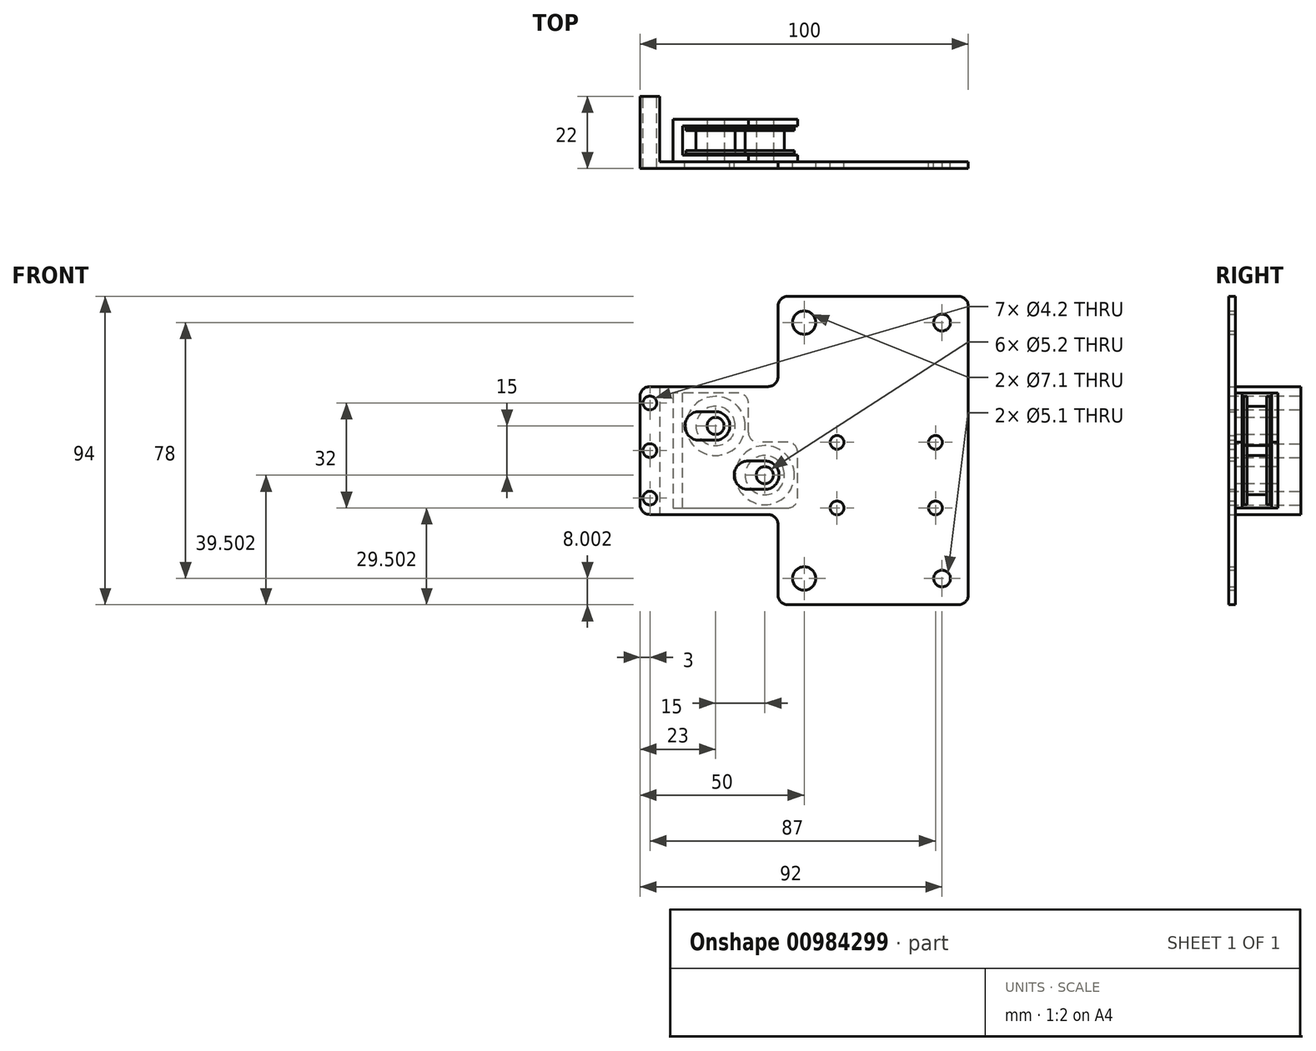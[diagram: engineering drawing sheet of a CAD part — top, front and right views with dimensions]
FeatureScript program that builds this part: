
annotation { "Feature Type Name" : "Feature", "Feature Type Description" : "" }
export const myFeature = defineFeature(function(context is Context, id is Id, definition is map)
    precondition{}
    {
        {
            var Q0;
            Q0=qCreatedBy(makeId("Front.planeOp"),FACE);
            var sketch = newSketch(context, id + "F0", { "sketchPlane" : qUnion([Q0])});
            skCircle(sketch, "E0", {"center": v(-21, 47.4) * mm, "radius": 3.55 * mm});
            skCircle(sketch, "E1", {"center": v(-21, -30.6) * mm, "radius": 3.55 * mm});
            skCircle(sketch, "E2", {"center": v(21, -30.6) * mm, "radius": 2.55 * mm});
            skCircle(sketch, "E3", {"center": v(21, 47.4) * mm, "radius": 2.55 * mm});
            skCircle(sketch, "E4", {"center": v(-11, 10.9) * mm, "radius": 2.1 * mm});
            skCircle(sketch, "E5", {"center": v(-11, -9.1) * mm, "radius": 2.1 * mm});
            skCircle(sketch, "E6", {"center": v(19, -9.1) * mm, "radius": 2.1 * mm});
            skCircle(sketch, "E7", {"center": v(19, 10.9) * mm, "radius": 2.1 * mm});
            skLineSegment(sketch, "E8", {"start": v(26, 55.4) * mm, "end": v(-26, 55.4) * mm});
            skLineSegment(sketch, "E9", {"start": v(-29, 52.4) * mm, "end": v(-29, 30.9) * mm});
            skLineSegment(sketch, "E10", {"start": v(-32, 27.9) * mm, "end": v(-68, 27.9) * mm});
            skLineSegment(sketch, "E11", {"start": v(-71, 24.9) * mm, "end": v(-71, -8.1) * mm});
            skLineSegment(sketch, "E12", {"start": v(-68, -11.1) * mm, "end": v(-32, -11.1) * mm});
            skLineSegment(sketch, "E13", {"start": v(-29, -14.1) * mm, "end": v(-29, -35.6) * mm});
            skLineSegment(sketch, "E14", {"start": v(-26, -38.6) * mm, "end": v(26, -38.6) * mm});
            skLineSegment(sketch, "E15", {"start": v(29, -35.6) * mm, "end": v(29, 52.4) * mm});
            skArc(sketch, "E16", {"start": v(-53, 20.24) * mm, "mid": v(-57.35, 15.9) * mm, "end": v(-53, 11.54) * mm});
            skArc(sketch, "E17", {"start": v(-48, 11.54) * mm, "mid": v(-43.65, 15.9) * mm, "end": v(-48, 20.24) * mm});
            skLineSegment(sketch, "E18", {"start": v(-53, 11.54) * mm, "end": v(-48, 11.54) * mm});
            skLineSegment(sketch, "E19", {"start": v(-53, 20.24) * mm, "end": v(-48, 20.24) * mm});
            skArc(sketch, "E20", {"start": v(-38, 5.24) * mm, "mid": v(-42.35, 0.9) * mm, "end": v(-38, -3.46) * mm});
            skArc(sketch, "E21", {"start": v(-33, -3.46) * mm, "mid": v(-28.65, 0.9) * mm, "end": v(-33, 5.24) * mm});
            skLineSegment(sketch, "E22", {"start": v(-38, 5.24) * mm, "end": v(-33, 5.24) * mm});
            skLineSegment(sketch, "E23", {"start": v(-33, -3.46) * mm, "end": v(-38, -3.46) * mm});
            skCircle(sketch, "E24", {"center": v(-68, 22.9) * mm, "radius": 2.1 * mm});
            skCircle(sketch, "E25", {"center": v(-68, 8.4) * mm, "radius": 2.1 * mm});
            skCircle(sketch, "E26", {"center": v(-68, -6.1) * mm, "radius": 2.1 * mm});
            skPoint(sketch, "E27.visualSharp", {"position": v(-71, 27.9) * mm});
            skArc(sketch, "E27.filletArc", {"start": v(-68, 27.9) * mm, "mid": v(-70.12, 27.01) * mm, "end": v(-71, 24.9) * mm});
            skPoint(sketch, "E28.visualSharp", {"position": v(-71, -11.1) * mm});
            skArc(sketch, "E28.filletArc", {"start": v(-71, -8.1) * mm, "mid": v(-70.12, -10.23) * mm, "end": v(-68, -11.1) * mm});
            skPoint(sketch, "E29.visualSharp", {"position": v(-29, -11.1) * mm});
            skArc(sketch, "E29.filletArc", {"start": v(-29, -14.1) * mm, "mid": v(-29.88, -11.99) * mm, "end": v(-32, -11.1) * mm});
            skPoint(sketch, "E30.visualSharp", {"position": v(-29, -38.6) * mm});
            skArc(sketch, "E30.filletArc", {"start": v(-29, -35.6) * mm, "mid": v(-28.12, -37.73) * mm, "end": v(-26, -38.6) * mm});
            skPoint(sketch, "E31.visualSharp", {"position": v(29, -38.6) * mm});
            skArc(sketch, "E31.filletArc", {"start": v(26, -38.6) * mm, "mid": v(28.12, -37.73) * mm, "end": v(29, -35.6) * mm});
            skPoint(sketch, "E32.visualSharp", {"position": v(29, 55.4) * mm});
            skArc(sketch, "E32.filletArc", {"start": v(29, 52.4) * mm, "mid": v(28.12, 54.51) * mm, "end": v(26, 55.4) * mm});
            skPoint(sketch, "E33.visualSharp", {"position": v(-29, 55.4) * mm});
            skArc(sketch, "E33.filletArc", {"start": v(-26, 55.4) * mm, "mid": v(-28.12, 54.51) * mm, "end": v(-29, 52.4) * mm});
            skPoint(sketch, "E34.visualSharp", {"position": v(-29, 27.9) * mm});
            skArc(sketch, "E34.filletArc", {"start": v(-32, 27.9) * mm, "mid": v(-29.88, 28.77) * mm, "end": v(-29, 30.9) * mm});
            skLineSegment(sketch, "E35", {"start": v(-65, 27.9) * mm, "end": v(-65, -11.1) * mm});
            skSolve(sketch);
        }
        {
            var Q0;
            Q0=qCreatedBy(makeId("Front.planeOp"),FACE);
            var sketch = newSketch(context, id + "F1", { "sketchPlane" : qUnion([Q0])});
            skCircle(sketch, "E36", {"center": v(-48, 15.9) * mm, "radius": 9 * mm});
            skCircle(sketch, "E37", {"center": v(-33, 0.9) * mm, "radius": 9 * mm});
            skCircle(sketch, "E38", {"center": v(-33, 0.9) * mm, "radius": 6 * mm});
            skCircle(sketch, "E39", {"center": v(-48, 15.9) * mm, "radius": 6 * mm});
            skCircle(sketch, "E40", {"center": v(-48, 15.9) * mm, "radius": 2.6 * mm});
            skCircle(sketch, "E41", {"center": v(-33, 0.9) * mm, "radius": 2.6 * mm});
            skSolve(sketch);
        }
        {
            var Q0;
            Q0=makeQuery(id+"F1.imprint","IMPRINT",FACE,{"disambiguationData":[TD([[makeQuery(id+"F1.imprint","IMPRINT",EDGE,{"derivedFrom":sQuery(id+"F1.wireOp",EDGE,"E39")}),1.0]])]});
            var Q1;
            Q1=makeQuery(id+"F1.imprint","IMPRINT",FACE,{"disambiguationData":[TD([[makeQuery(id+"F1.imprint","IMPRINT",EDGE,{"derivedFrom":sQuery(id+"F1.wireOp",EDGE,"E36")}),1.0]])]});
            var Q2;
            Q2=makeQuery(id+"F1.imprint","IMPRINT",FACE,{"disambiguationData":[TD([[makeQuery(id+"F1.imprint","IMPRINT",EDGE,{"derivedFrom":sQuery(id+"F1.wireOp",EDGE,"E38")}),1.0]])]});
            var Q3;
            Q3=makeQuery(id+"F1.imprint","IMPRINT",FACE,{"disambiguationData":[TD([[makeQuery(id+"F1.imprint","IMPRINT",EDGE,{"derivedFrom":sQuery(id+"F1.wireOp",EDGE,"E37")}),1.0]])]});
            extrude(context, id + "F2", {"entities" : qUnion([Q0, Q1, Q2, Q3]), "oppositeDirection" : true, "depth" : 3.5 * mm, "offsetDistance" : 25 * mm, "hasSecondDirection" : true, "secondDirectionOppositeDirection" : true, "secondDirectionDepth" : 2.5 * mm});
        }
        {
            var Q0;
            Q0=makeQuery(id+"F1.imprint","IMPRINT",FACE,{"disambiguationData":[TD([[makeQuery(id+"F1.imprint","IMPRINT",EDGE,{"derivedFrom":sQuery(id+"F1.wireOp",EDGE,"E39")}),1.0]])]});
            var Q1;
            Q1=makeQuery(id+"F1.imprint","IMPRINT",FACE,{"disambiguationData":[TD([[makeQuery(id+"F1.imprint","IMPRINT",EDGE,{"derivedFrom":sQuery(id+"F1.wireOp",EDGE,"E38")}),1.0]])]});
            extrude(context, id + "F3", {"entities" : qUnion([Q0, Q1]), "operationType" : NewBodyOperationType.ADD, "oppositeDirection" : true, "depth" : 9.5 * mm, "offsetDistance" : 25 * mm, "hasSecondDirection" : true, "secondDirectionOppositeDirection" : true, "secondDirectionDepth" : 3.5 * mm});
        }
        {
            var Q0;
            Q0=makeQuery(id+"F1.imprint","IMPRINT",FACE,{"disambiguationData":[TD([[makeQuery(id+"F1.imprint","IMPRINT",EDGE,{"derivedFrom":sQuery(id+"F1.wireOp",EDGE,"E36")}),1.0]])]});
            var Q1;
            Q1=makeQuery(id+"F1.imprint","IMPRINT",FACE,{"disambiguationData":[TD([[makeQuery(id+"F1.imprint","IMPRINT",EDGE,{"derivedFrom":sQuery(id+"F1.wireOp",EDGE,"E39")}),1.0]])]});
            var Q2;
            Q2=makeQuery(id+"F1.imprint","IMPRINT",FACE,{"disambiguationData":[TD([[makeQuery(id+"F1.imprint","IMPRINT",EDGE,{"derivedFrom":sQuery(id+"F1.wireOp",EDGE,"E38")}),1.0]])]});
            var Q3;
            Q3=makeQuery(id+"F1.imprint","IMPRINT",FACE,{"disambiguationData":[TD([[makeQuery(id+"F1.imprint","IMPRINT",EDGE,{"derivedFrom":sQuery(id+"F1.wireOp",EDGE,"E37")}),1.0]])]});
            extrude(context, id + "F4", {"entities" : qUnion([Q0, Q1, Q2, Q3]), "operationType" : NewBodyOperationType.ADD, "oppositeDirection" : true, "depth" : 10.5 * mm, "offsetDistance" : 25 * mm, "hasSecondDirection" : true, "secondDirectionOppositeDirection" : true, "secondDirectionDepth" : 9.5 * mm});
        }
        {
            var Q0;
            Q0=makeQuery(id+"F0.imprint","IMPRINT",FACE,{"disambiguationData":[TD([[makeQuery(id+"F0.imprint","IMPRINT",EDGE,{"derivedFrom":sQuery(id+"F0.wireOp",EDGE,"E0")}),-1.0]])]});
            var Q1;
            Q1=makeQuery(id+"F0.imprint","IMPRINT",FACE,{"disambiguationData":[TD([[makeQuery(id+"F0.imprint","IMPRINT",EDGE,{"derivedFrom":sQuery(id+"F0.wireOp",EDGE,"E11")}),1.0]])]});
            extrude(context, id + "F5", {"entities" : qUnion([Q0, Q1]), "depth" : 2 * mm, "offsetDistance" : 25 * mm});
        }
        {
            var Q0;
            Q0=makeQuery(id+"F0.imprint","IMPRINT",FACE,{"disambiguationData":[TD([[makeQuery(id+"F0.imprint","IMPRINT",EDGE,{"derivedFrom":sQuery(id+"F0.wireOp",EDGE,"E11")}),1.0]])]});
            extrude(context, id + "F6", {"entities" : qUnion([Q0]), "operationType" : NewBodyOperationType.ADD, "oppositeDirection" : true, "depth" : 20 * mm, "offsetDistance" : 25 * mm});
        }
        {
            var Q0;
            Q0=qCreatedBy(makeId("Front.planeOp"),FACE);
            var sketch = newSketch(context, id + "F7", { "sketchPlane" : qUnion([Q0])});
            skLineSegment(sketch, "E42", {"start": v(-58, 25.9) * mm, "end": v(-58, -9.1) * mm});
            skLineSegment(sketch, "E43", {"start": v(-58, -9.1) * mm, "end": v(-26, -9.1) * mm});
            skLineSegment(sketch, "E44", {"start": v(-23, -6.1) * mm, "end": v(-23, 7.9) * mm});
            skLineSegment(sketch, "E45", {"start": v(-26, 10.9) * mm, "end": v(-35, 10.9) * mm});
            skLineSegment(sketch, "E46", {"start": v(-38, 13.9) * mm, "end": v(-38, 22.9) * mm});
            skLineSegment(sketch, "E47", {"start": v(-41, 25.9) * mm, "end": v(-58, 25.9) * mm});
            skLineSegment(sketch, "E48", {"start": v(-58, 25.9) * mm, "end": v(-61, 25.9) * mm});
            skLineSegment(sketch, "E49", {"start": v(-61, 25.9) * mm, "end": v(-61, -9.1) * mm});
            skLineSegment(sketch, "E50", {"start": v(-61, -9.1) * mm, "end": v(-58, -9.1) * mm});
            skCircle(sketch, "E51", {"center": v(-48, 15.9) * mm, "radius": 2.6 * mm});
            skCircle(sketch, "E52", {"center": v(-33, 0.9) * mm, "radius": 2.6 * mm});
            skPoint(sketch, "E53.visualSharp", {"position": v(-23, 10.9) * mm});
            skArc(sketch, "E53.filletArc", {"start": v(-23, 7.9) * mm, "mid": v(-23.88, 10.01) * mm, "end": v(-26, 10.9) * mm});
            skPoint(sketch, "E54.visualSharp", {"position": v(-23, -9.1) * mm});
            skArc(sketch, "E54.filletArc", {"start": v(-26, -9.1) * mm, "mid": v(-23.88, -8.23) * mm, "end": v(-23, -6.1) * mm});
            skPoint(sketch, "E55.visualSharp", {"position": v(-38, 25.9) * mm});
            skArc(sketch, "E55.filletArc", {"start": v(-38, 22.9) * mm, "mid": v(-38.88, 25.01) * mm, "end": v(-41, 25.9) * mm});
            skPoint(sketch, "E56.visualSharp", {"position": v(-38, 10.9) * mm});
            skArc(sketch, "E56.filletArc", {"start": v(-38, 13.9) * mm, "mid": v(-37.12, 11.77) * mm, "end": v(-35, 10.9) * mm});
            skSolve(sketch);
        }
        {
            var Q0;
            Q0=makeQuery(id+"F7.imprint","IMPRINT",FACE,{"disambiguationData":[TD([[makeQuery(id+"F7.imprint","IMPRINT",EDGE,{"derivedFrom":sQuery(id+"F7.wireOp",EDGE,"E42")}),-1.0]])]});
            extrude(context, id + "F8", {"entities" : qUnion([Q0]), "oppositeDirection" : true, "depth" : 13 * mm, "offsetDistance" : 25 * mm});
        }
        {
            var Q0;
            Q0=makeQuery(id+"F7.imprint","IMPRINT",FACE,{"disambiguationData":[TD([[makeQuery(id+"F7.imprint","IMPRINT",EDGE,{"derivedFrom":sQuery(id+"F7.wireOp",EDGE,"E42")}),1.0]])]});
            var Q1;
            Q1=makeQuery(id+"F7.imprint","IMPRINT",FACE,{"disambiguationData":[TD([[makeQuery(id+"F7.imprint","IMPRINT",EDGE,{"derivedFrom":sQuery(id+"F7.wireOp",EDGE,"E42")}),-1.0]])]});
            extrude(context, id + "F9", {"entities" : qUnion([Q0, Q1]), "operationType" : NewBodyOperationType.ADD, "oppositeDirection" : true, "depth" : 2 * mm, "offsetDistance" : 25 * mm});
        }
        {
            var Q0;
            Q0=makeQuery(id+"F7.imprint","IMPRINT",FACE,{"disambiguationData":[TD([[makeQuery(id+"F7.imprint","IMPRINT",EDGE,{"derivedFrom":sQuery(id+"F7.wireOp",EDGE,"E42")}),1.0]])]});
            var Q1;
            Q1=makeQuery(id+"F7.imprint","IMPRINT",FACE,{"disambiguationData":[TD([[makeQuery(id+"F7.imprint","IMPRINT",EDGE,{"derivedFrom":sQuery(id+"F7.wireOp",EDGE,"E42")}),-1.0]])]});
            extrude(context, id + "F10", {"entities" : qUnion([Q0, Q1]), "operationType" : NewBodyOperationType.ADD, "oppositeDirection" : true, "depth" : 13 * mm, "offsetDistance" : 25 * mm, "hasSecondDirection" : true, "secondDirectionOppositeDirection" : true, "secondDirectionDepth" : 11 * mm});
        }
    });
